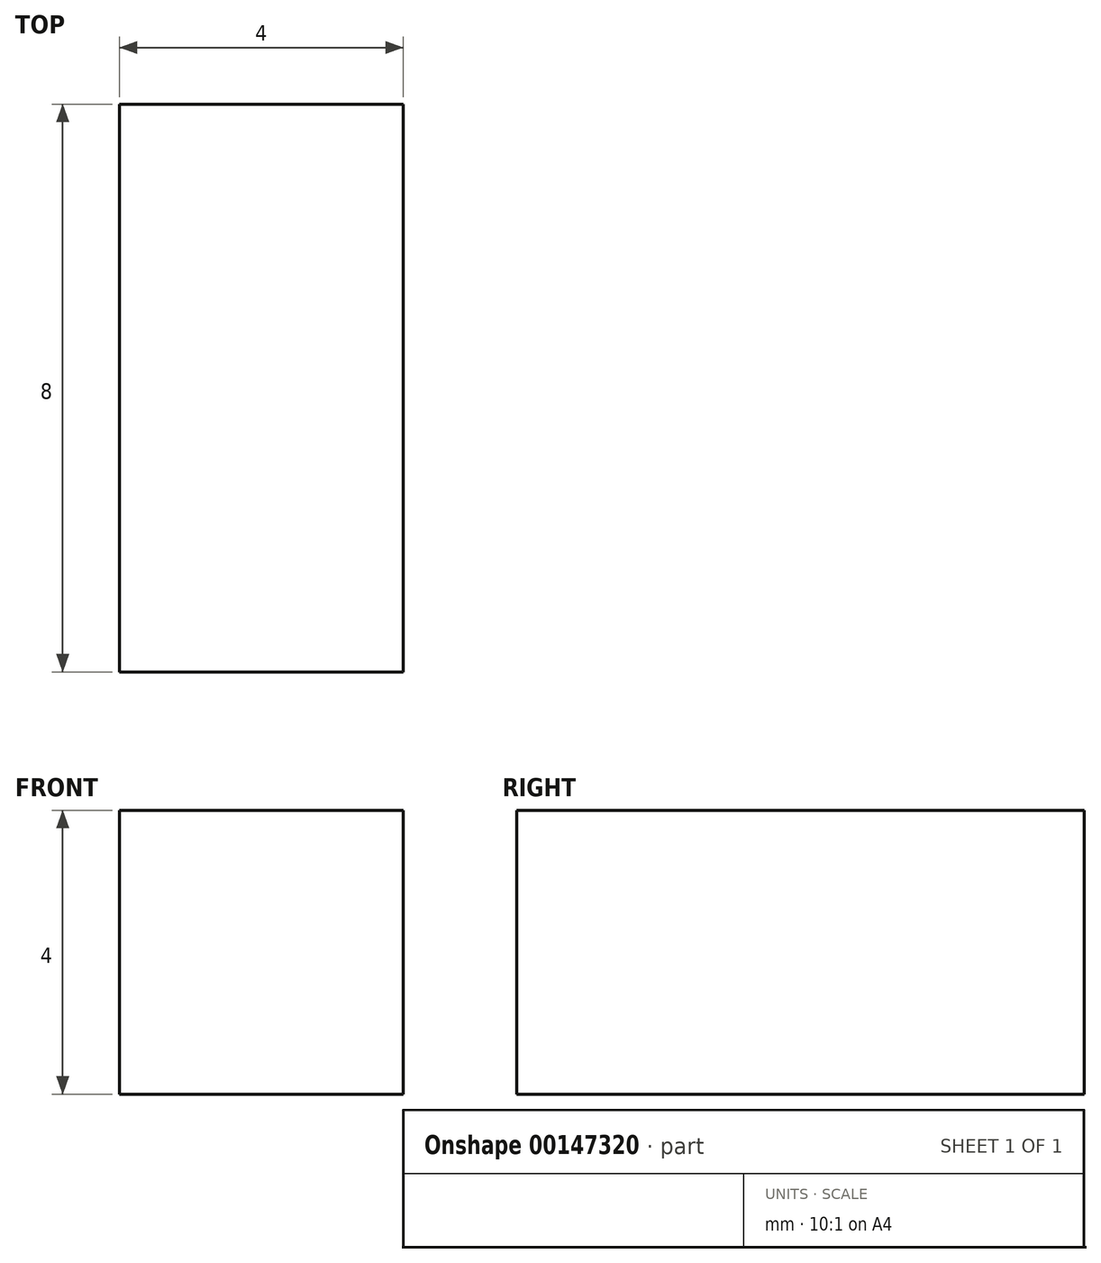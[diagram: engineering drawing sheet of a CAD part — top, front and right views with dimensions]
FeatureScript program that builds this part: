
annotation { "Feature Type Name" : "Feature", "Feature Type Description" : "" }
export const myFeature = defineFeature(function(context is Context, id is Id, definition is map)
    precondition{}
    {
        {
            var Q0;
            Q0=qCreatedBy(makeId("Front.planeOp"),FACE);
            var sketch = newSketch(context, id + "F0", { "sketchPlane" : qUnion([Q0])});
            skLineSegment(sketch, "E0.bottom", {"start": v(0, 0) * mm, "end": v(4, 0) * mm});
            skLineSegment(sketch, "E0.top", {"start": v(0, 4) * mm, "end": v(4, 4) * mm});
            skLineSegment(sketch, "E0.left", {"start": v(0, 0) * mm, "end": v(0, 4) * mm});
            skLineSegment(sketch, "E0.right", {"start": v(4, 0) * mm, "end": v(4, 4) * mm});
            skSolve(sketch);
        }
        {
            var Q0;
            Q0 = qSketchRegion(id + "F0", true);
            extrude(context, id + "F1", {"entities" : qUnion([Q0]), "depth" : 8 * mm});
        }
    });
